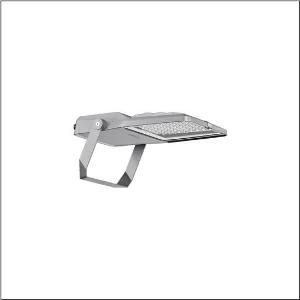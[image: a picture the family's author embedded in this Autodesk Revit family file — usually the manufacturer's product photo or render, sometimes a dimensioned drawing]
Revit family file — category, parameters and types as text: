
# Revit family: floodlight_fl_21_iq_mini___pl52_5xa7771d2d1a_936e
name_source: partatom
category: Lighting Fixtures
units: mm (PartAtom-declared; Revit-internal decimal feet)

## family parameters
Cut with Voids When Loaded = No
Host = Face
Light Source = No
Part Type = Normal
Room Calculation Point = No
Round Connector Dimension = Use Diameter
Shared = No

## types (1)
- --- (1 x LED, 17830 lm, 143 W, 3000K)
    Apparent Load = 143 VA
    CIE Flux Codes = 26 60 98 100 100
    Color Rendering = 70
    Color Temperature = 3000K
    Default Elevation = 1800 mm
    Description = Floodlight FL 21 iQ mini, floodlight, primary light control with lens, of PMMA, primary optical cover: protective disc, of toughened safety glass, transparent, light distribution: PL52, light emission: direct distribution, installation type: surface-mounted, LED, High Power LED, rated luminous flux: 17.830lm, luminous efficacy: 125lm/W, light colour: 730, colour temperature: 3000K, control: Auto-Match, Temp-Guard, Lumen-Switch, Night-Set, Smart-Wire, Light-Fading, Desk-Remote (wireless, voltage-free reading and setting of iQ features in the workshop via application-optimized NFC function/RFID function), optimised constant luminous flux control (CLO 2.0), with terminal, 6-pole, mains connection: 220..240V, AC, 50/60Hz, start of lifetime: 143W, end of service life: 152W, reduction: 61W, luminaire housing, of diecast aluminium, powder-coated, Siteco® metallic grey (DB 702S), corrosivity category C5 mid according to DIN EN ISO 12944, sealing non-destructively replaceable, mounting bracket, of steel, galvanised, powder-coated, Siteco® metallic grey (DB 702S), protection rating (complete): IP66, insulation class (complete): insulation class II (safety insulation), certification: CE, ENEC, VDE, protection symbol: D, impact resistance: IK08, permissible operating ambient temperature: -40..+40°C, permissible operating ambient temperature for outdoor applications: -40..+50°C, standard: DIN EN 12944, LABS conformity tested according to VDMA 24364:2018-05, packaging unit: 1 piece

Light Distribution: PL52
    Height = 70 mm
    Lamp = 1 x LED
    Lamp Light Flux = 17830 lm
    Lamp Power = 143 W
    Lamp count = 1
    Length = 485 mm
    Luminous efficacy = 125 lm/W
    Manufacturer = Siteco
    ModVariant = No
    Model = 5XA7771D2D1A
    Number of Poles = 1
    OnlyDefault = Yes
    Power Factor = 1
    Product Name = Floodlight FL 21 iQ mini | PL52
    Product group = floodlight | pylon annexe
    ProductGroupID = 6200
    Protection Class = Protection class II
    Protection Degree = IP 66
    RLX_Detail_Level = 1
    RLX_Emergency_Light_Flux = 0 lm
    RLX_Emergency_Type = 0
    RLX_Emergency_Type_DB = No
    RlxData = <blob elided: 96637 chars, md5=4fc9545c>
    Socket = socket
    Standby Power = 0 W
    System Light Flux = 17830 lm
    System Power = 143 W
    Type Comments = factory setting: luminous flux: 100 % | dim-lin: 254 | 730 mA
    Type Image = l_1006845.jpg
    URL = http://relux.com
    VarID = @adj_114205
    Voltage = 0 V
    Weight = 0.00 kg
    Width = 337 mm

## geometry (parser evidence)
native form markers: Blend x4, Sweep x13
no freeform markers — native parametric forms only
